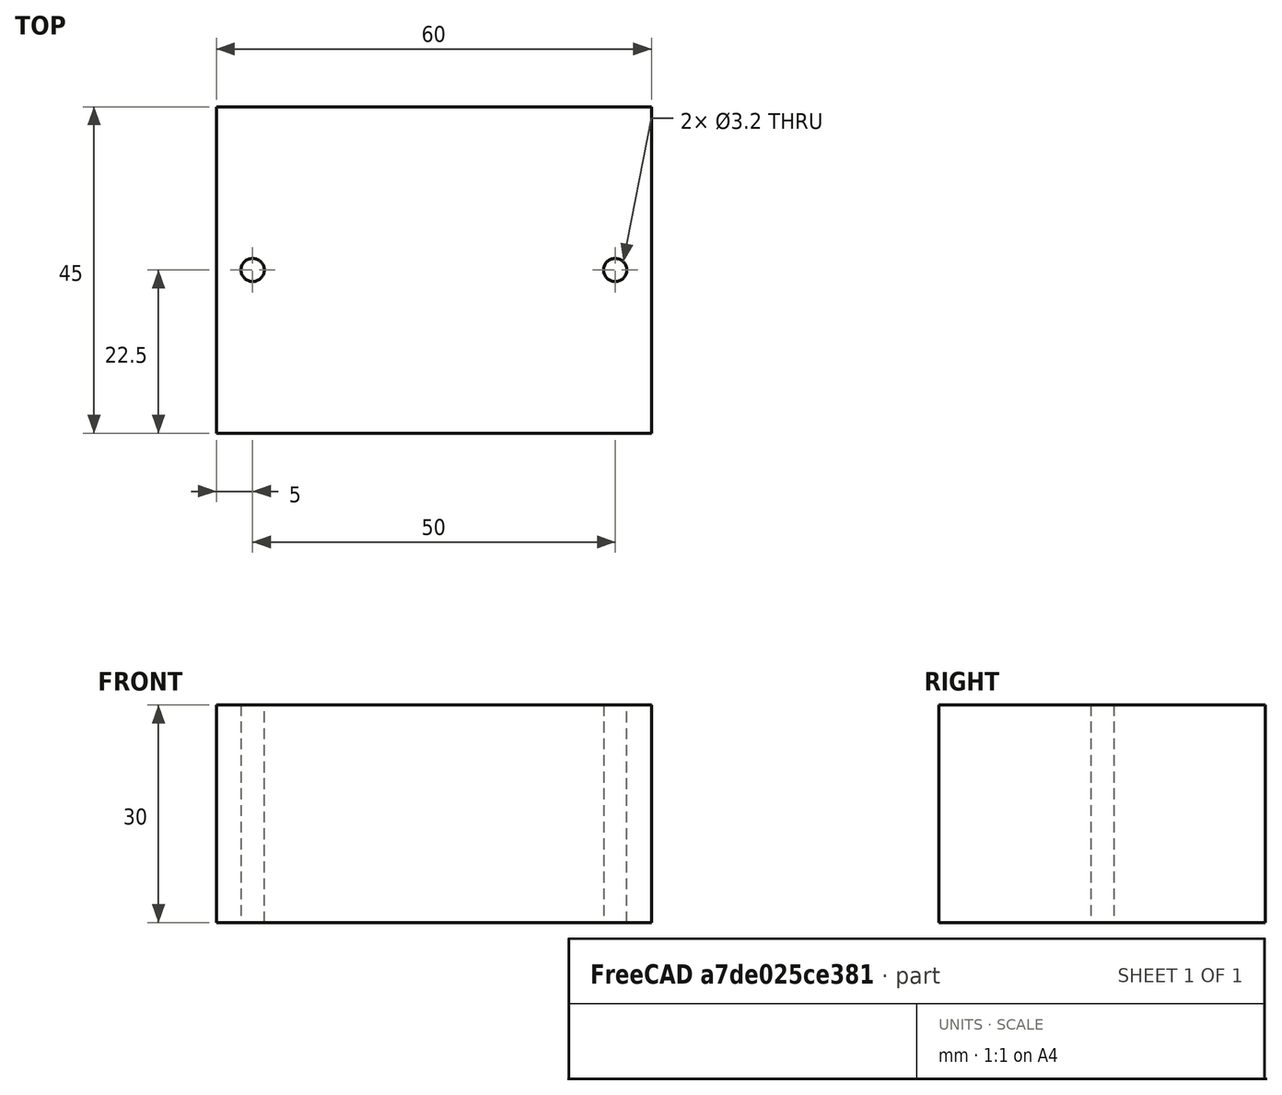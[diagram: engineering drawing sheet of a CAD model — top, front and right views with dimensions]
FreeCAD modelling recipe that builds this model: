
FCSTD DOCUMENT  (FreeCAD 0.18R16131 (Git))
Label: Relay
License: All rights reserved
LicenseURL: http://en.wikipedia.org/wiki/All_rights_reserved
objects: Sketcher::SketchObject×1, PartDesign::Pad×1, PartDesign::Body×1, App::Part×1
note: 4 computed .brp shape members not serialized (recipe doc carries the construction recipe); baked Part::Feature solids carry a one-line shape summary decoded from their .brp

FEATURE [Sketcher::SketchObject] Sketch  label="RelaySketch"
  MapMode = 5
  Support = -> [XY_Plane001]
  sketch-geometry (7):
    g0: LineSegment StartX=0 StartY=0 StartZ=0 EndX=60 EndY=0 EndZ=0
    g1: LineSegment StartX=60 StartY=0 StartZ=0 EndX=60 EndY=45 EndZ=0
    g2: LineSegment StartX=60 StartY=45 StartZ=0 EndX=0 EndY=45 EndZ=0
    g3: LineSegment StartX=0 StartY=45 StartZ=0 EndX=0 EndY=0 EndZ=0
    g4: Circle CenterX=5 CenterY=22.5 CenterZ=0 NormalX=0 NormalY=0 NormalZ=1 AngleXU=0 Radius=1.6
    g5: Circle CenterX=55 CenterY=22.5 CenterZ=0 NormalX=0 NormalY=0 NormalZ=1 AngleXU=0 Radius=1.6
    g6: LineSegment [constr] StartX=5 StartY=22.5 StartZ=0 EndX=55 EndY=22.5 EndZ=0
  constraints (19):
    c: Coincident(g0,g1)
    c: Coincident(g1,g2)
    c: Coincident(g2,g3)
    c: Coincident(g3,g0)
    c: Horizontal(g0)
    c: Horizontal(g2)
    c: Vertical(g1)
    c: Vertical(g3)
    c: Coincident(g0,g-1)
    c: Coincident(g6,g4)
    c: Coincident(g6,g5)
    c: Horizontal(g6)
    c: Equal(g4,g5)
    c: Radius(g4) = 1.6
    c: Distance(g3) = 45
    c: Distance(g2) = 60
    c: Distance(g6) = 50
    c: Distance(g4,g3) = 5
    c: Distance(g4,g0) = 22.5
FEATURE [PartDesign::Pad] Pad  label="RelayPad"
  Length = 30
  Length2 = 100
  Profile = -> Sketch
  Type = 0
FEATURE [PartDesign::Body] Body  label="RelayBody"
  Group = -> [Sketch,Pad]
  Origin = -> Origin001
  Tip = -> Pad
FEATURE [App::Part] Part  label="RelayPart"
  Group = -> [Body]
  Origin = -> Origin
